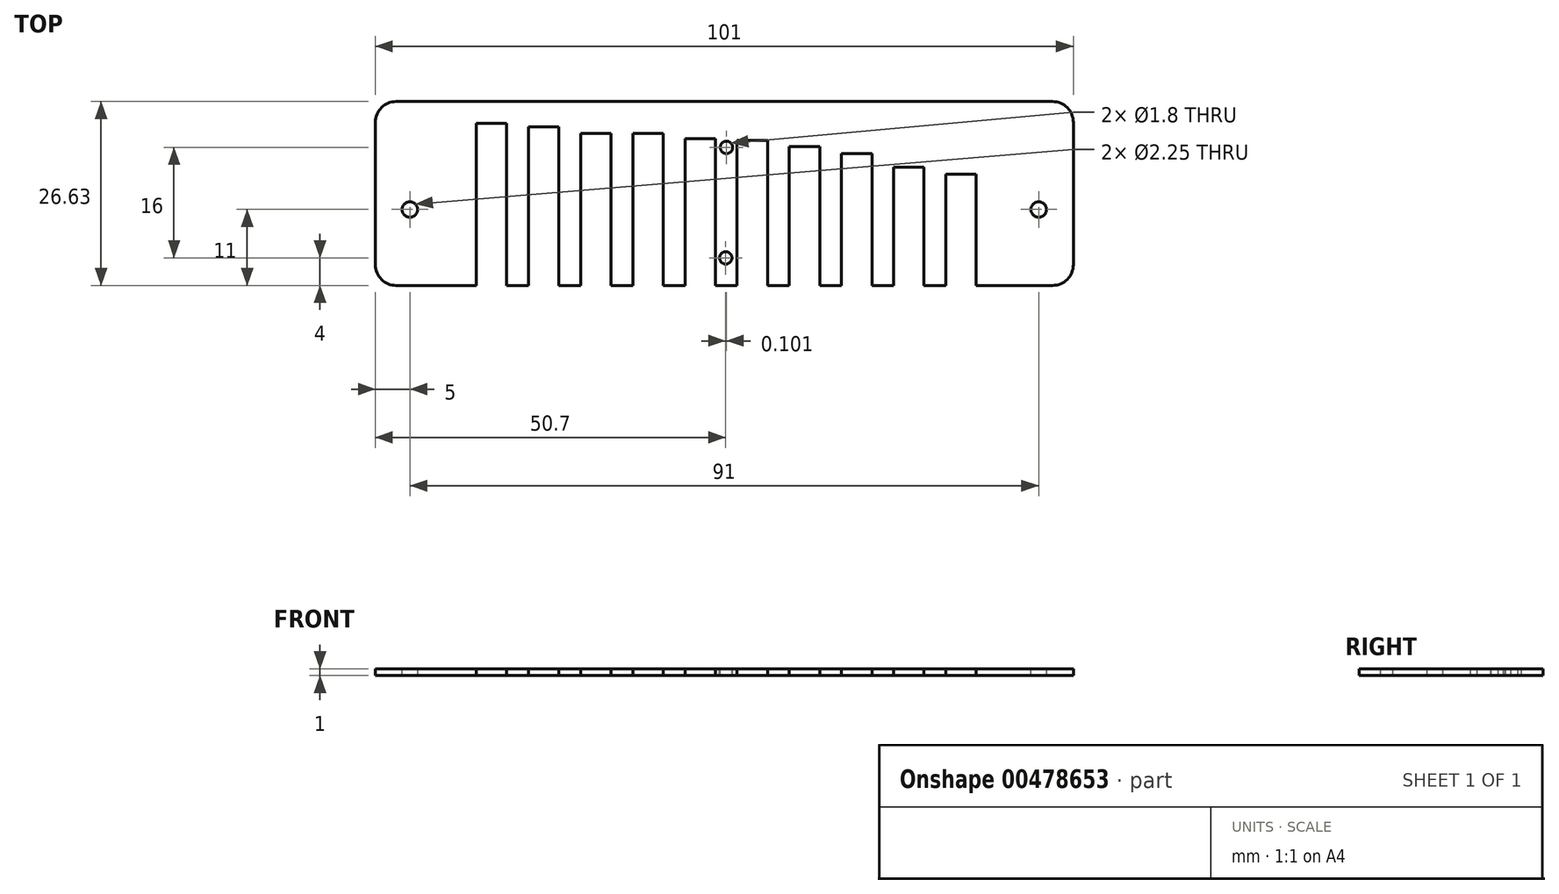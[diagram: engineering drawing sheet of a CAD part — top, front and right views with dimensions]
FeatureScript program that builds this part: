
annotation { "Feature Type Name" : "Feature", "Feature Type Description" : "" }
export const myFeature = defineFeature(function(context is Context, id is Id, definition is map)
    precondition{}
    {
        {
            var Q0;
            Q0=qCreatedBy(makeId("Right.planeOp"),FACE);
            var sketch = newSketch(context, id + "F0", { "sketchPlane" : qUnion([Q0])});
            skLineSegment(sketch, "E0.bottom", {"start": v(3, 0) * mm, "end": v(98, 0) * mm});
            skLineSegment(sketch, "E0.top", {"start": v(3, 26.63) * mm, "end": v(98, 26.63) * mm});
            skLineSegment(sketch, "E0.left", {"start": v(0, 3) * mm, "end": v(0, 23.63) * mm});
            skLineSegment(sketch, "E0.right", {"start": v(101, 3) * mm, "end": v(101, 23.63) * mm});
            skLineSegment(sketch, "E1.bottom", {"start": v(14.6, 26.63) * mm, "end": v(19, 26.63) * mm});
            skLineSegment(sketch, "E1.top", {"start": v(14.6, 3.13) * mm, "end": v(19, 3.13) * mm});
            skLineSegment(sketch, "E1.left", {"start": v(14.6, 26.63) * mm, "end": v(14.6, 3.13) * mm});
            skLineSegment(sketch, "E1.right", {"start": v(19, 26.63) * mm, "end": v(19, 3.13) * mm});
            skLineSegment(sketch, "E2.bottom", {"start": v(22.15, 26.63) * mm, "end": v(26.55, 26.63) * mm});
            skLineSegment(sketch, "E2.top", {"start": v(22.15, 3.63) * mm, "end": v(26.55, 3.63) * mm});
            skLineSegment(sketch, "E2.left", {"start": v(22.15, 26.63) * mm, "end": v(22.15, 3.63) * mm});
            skLineSegment(sketch, "E2.right", {"start": v(26.55, 26.63) * mm, "end": v(26.55, 3.63) * mm});
            skLineSegment(sketch, "E3.bottom", {"start": v(29.7, 26.63) * mm, "end": v(34.1, 26.63) * mm});
            skLineSegment(sketch, "E3.top", {"start": v(29.7, 4.63) * mm, "end": v(34.1, 4.63) * mm});
            skLineSegment(sketch, "E3.left", {"start": v(29.7, 26.63) * mm, "end": v(29.7, 4.63) * mm});
            skLineSegment(sketch, "E3.right", {"start": v(34.1, 26.63) * mm, "end": v(34.1, 4.63) * mm});
            skLineSegment(sketch, "E4.bottom", {"start": v(37.25, 26.63) * mm, "end": v(41.65, 26.63) * mm});
            skLineSegment(sketch, "E4.top", {"start": v(37.25, 4.63) * mm, "end": v(41.65, 4.63) * mm});
            skLineSegment(sketch, "E4.left", {"start": v(37.25, 26.63) * mm, "end": v(37.25, 4.63) * mm});
            skLineSegment(sketch, "E4.right", {"start": v(41.65, 26.63) * mm, "end": v(41.65, 4.63) * mm});
            skLineSegment(sketch, "E5.bottom", {"start": v(44.8, 26.63) * mm, "end": v(49.2, 26.63) * mm});
            skLineSegment(sketch, "E5.top", {"start": v(44.8, 5.4) * mm, "end": v(49.2, 5.4) * mm});
            skLineSegment(sketch, "E5.left", {"start": v(44.8, 26.63) * mm, "end": v(44.8, 5.4) * mm});
            skLineSegment(sketch, "E5.right", {"start": v(49.2, 26.63) * mm, "end": v(49.2, 5.4) * mm});
            skLineSegment(sketch, "E6.bottom", {"start": v(52.35, 26.63) * mm, "end": v(56.75, 26.63) * mm});
            skLineSegment(sketch, "E6.top", {"start": v(52.35, 5.63) * mm, "end": v(56.75, 5.63) * mm});
            skLineSegment(sketch, "E6.left", {"start": v(52.35, 26.63) * mm, "end": v(52.35, 5.63) * mm});
            skLineSegment(sketch, "E6.right", {"start": v(56.75, 26.63) * mm, "end": v(56.75, 5.63) * mm});
            skLineSegment(sketch, "E7.bottom", {"start": v(59.9, 26.63) * mm, "end": v(64.3, 26.63) * mm});
            skLineSegment(sketch, "E7.top", {"start": v(59.9, 6.5) * mm, "end": v(64.3, 6.5) * mm});
            skLineSegment(sketch, "E7.left", {"start": v(59.9, 26.63) * mm, "end": v(59.9, 6.5) * mm});
            skLineSegment(sketch, "E7.right", {"start": v(64.3, 26.63) * mm, "end": v(64.3, 6.5) * mm});
            skLineSegment(sketch, "E8.bottom", {"start": v(67.45, 26.63) * mm, "end": v(71.85, 26.63) * mm});
            skLineSegment(sketch, "E8.top", {"start": v(67.45, 7.56) * mm, "end": v(71.85, 7.56) * mm});
            skLineSegment(sketch, "E8.left", {"start": v(67.45, 26.63) * mm, "end": v(67.45, 7.56) * mm});
            skLineSegment(sketch, "E8.right", {"start": v(71.85, 26.63) * mm, "end": v(71.85, 7.56) * mm});
            skLineSegment(sketch, "E9.bottom", {"start": v(75, 26.63) * mm, "end": v(79.4, 26.63) * mm});
            skLineSegment(sketch, "E9.top", {"start": v(75, 9.52) * mm, "end": v(79.4, 9.52) * mm});
            skLineSegment(sketch, "E9.left", {"start": v(75, 26.63) * mm, "end": v(75, 9.52) * mm});
            skLineSegment(sketch, "E9.right", {"start": v(79.4, 26.63) * mm, "end": v(79.4, 9.52) * mm});
            skLineSegment(sketch, "E10.bottom", {"start": v(82.55, 26.63) * mm, "end": v(86.95, 26.63) * mm});
            skLineSegment(sketch, "E10.top", {"start": v(82.55, 10.52) * mm, "end": v(86.95, 10.52) * mm});
            skLineSegment(sketch, "E10.left", {"start": v(82.55, 26.63) * mm, "end": v(82.55, 10.52) * mm});
            skLineSegment(sketch, "E10.right", {"start": v(86.95, 26.63) * mm, "end": v(86.95, 10.52) * mm});
            skPoint(sketch, "E11.visualSharp", {"position": v(0, 26.63) * mm});
            skArc(sketch, "E11.filletArc", {"start": v(3, 26.63) * mm, "mid": v(0.88, 25.75) * mm, "end": v(0, 23.63) * mm});
            skPoint(sketch, "E12.visualSharp", {"position": v(0, 0) * mm});
            skArc(sketch, "E12.filletArc", {"start": v(0, 3) * mm, "mid": v(0.88, 0.88) * mm, "end": v(3, 0) * mm});
            skPoint(sketch, "E13.visualSharp", {"position": v(101, 26.63) * mm});
            skArc(sketch, "E13.filletArc", {"start": v(101, 23.63) * mm, "mid": v(100.12, 25.75) * mm, "end": v(98, 26.63) * mm});
            skPoint(sketch, "E14.visualSharp", {"position": v(101, 0) * mm});
            skArc(sketch, "E14.filletArc", {"start": v(98, 0) * mm, "mid": v(100.12, 0.88) * mm, "end": v(101, 3) * mm});
            skPoint(sketch, "E15", {"position": v(5, 15.63) * mm});
            skPoint(sketch, "E16", {"position": v(50.7, 22.63) * mm});
            skCircle(sketch, "E17", {"center": v(5, 15.63) * mm, "radius": 1.13 * mm});
            skCircle(sketch, "E18", {"center": v(96, 15.63) * mm, "radius": 1.13 * mm});
            skCircle(sketch, "E19", {"center": v(50.7, 22.63) * mm, "radius": 0.9 * mm});
            skPoint(sketch, "E20", {"position": v(50.8, 6.63) * mm});
            skCircle(sketch, "E21", {"center": v(50.8, 6.63) * mm, "radius": 0.9 * mm});
            skSolve(sketch);
        }
        {
            var Q0;
            Q0=makeQuery(id+"F0.imprint","IMPRINT",FACE,{"disambiguationData":[TD([[makeQuery(id+"F0.imprint","IMPRINT",EDGE,{"derivedFrom":sQuery(id+"F0.wireOp",EDGE,"E0.bottom")}),1.0]])]});
            extrude(context, id + "F1", {"entities" : qUnion([Q0]), "depth" : 1 * mm});
        }
        {
            var Q0;
            Q0=makeQuery(id+"F1.opExtrude","SWEPT_BODY",BODY,{"disambiguationData":[OSD([sQuery(id+"F0.wireOp",EDGE,"E0.bottom"),sQuery(id+"F0.wireOp",EDGE,"E0.top"),sQuery(id+"F0.wireOp",EDGE,"E0.left"),sQuery(id+"F0.wireOp",EDGE,"E0.right"),sQuery(id+"F0.wireOp",EDGE,"E1.top"),sQuery(id+"F0.wireOp",EDGE,"E1.left"),sQuery(id+"F0.wireOp",EDGE,"E1.right"),sQuery(id+"F0.wireOp",EDGE,"E2.top"),sQuery(id+"F0.wireOp",EDGE,"E2.left"),sQuery(id+"F0.wireOp",EDGE,"E2.right"),sQuery(id+"F0.wireOp",EDGE,"E3.top"),sQuery(id+"F0.wireOp",EDGE,"E3.left"),sQuery(id+"F0.wireOp",EDGE,"E3.right"),sQuery(id+"F0.wireOp",EDGE,"E4.top"),sQuery(id+"F0.wireOp",EDGE,"E4.left"),sQuery(id+"F0.wireOp",EDGE,"E4.right"),sQuery(id+"F0.wireOp",EDGE,"E5.top"),sQuery(id+"F0.wireOp",EDGE,"E5.left"),sQuery(id+"F0.wireOp",EDGE,"E5.right"),sQuery(id+"F0.wireOp",EDGE,"E6.top"),sQuery(id+"F0.wireOp",EDGE,"E6.left"),sQuery(id+"F0.wireOp",EDGE,"E6.right"),sQuery(id+"F0.wireOp",EDGE,"E7.top"),sQuery(id+"F0.wireOp",EDGE,"E7.left"),sQuery(id+"F0.wireOp",EDGE,"E7.right"),sQuery(id+"F0.wireOp",EDGE,"E8.top"),sQuery(id+"F0.wireOp",EDGE,"E8.left"),sQuery(id+"F0.wireOp",EDGE,"E8.right"),sQuery(id+"F0.wireOp",EDGE,"E9.top"),sQuery(id+"F0.wireOp",EDGE,"E9.left"),sQuery(id+"F0.wireOp",EDGE,"E9.right"),sQuery(id+"F0.wireOp",EDGE,"E10.top"),sQuery(id+"F0.wireOp",EDGE,"E10.left"),sQuery(id+"F0.wireOp",EDGE,"E10.right"),sQuery(id+"F0.wireOp",EDGE,"E11.filletArc"),sQuery(id+"F0.wireOp",EDGE,"E12.filletArc"),sQuery(id+"F0.wireOp",EDGE,"E13.filletArc"),sQuery(id+"F0.wireOp",EDGE,"E14.filletArc"),sQuery(id+"F0.wireOp",EDGE,"E17"),sQuery(id+"F0.wireOp",EDGE,"E18"),sQuery(id+"F0.wireOp",EDGE,"E19"),sQuery(id+"F0.wireOp",EDGE,"E21")])]});
            var Q1;
            Q1=makeQuery(id+"F1.opExtrude","CAP_EDGE",EDGE,{"disambiguationData":[OSD([sQuery(id+"F0.wireOp",EDGE,"E0.bottom")])],"isStart":false});
            transform(context, id + "F2", {"entities" : qUnion([Q0]), "transformType" : TransformType.ROTATION, "transformAxis" : qUnion([Q1]), "angle" : 90 * degree, "makeCopy" : false});
        }
        {
            var Q0;
            Q0=makeQuery(id+"F1.opExtrude","SWEPT_BODY",BODY,{"disambiguationData":[OSD([sQuery(id+"F0.wireOp",EDGE,"E0.bottom"),sQuery(id+"F0.wireOp",EDGE,"E0.top"),sQuery(id+"F0.wireOp",EDGE,"E0.left"),sQuery(id+"F0.wireOp",EDGE,"E0.right"),sQuery(id+"F0.wireOp",EDGE,"E1.top"),sQuery(id+"F0.wireOp",EDGE,"E1.left"),sQuery(id+"F0.wireOp",EDGE,"E1.right"),sQuery(id+"F0.wireOp",EDGE,"E2.top"),sQuery(id+"F0.wireOp",EDGE,"E2.left"),sQuery(id+"F0.wireOp",EDGE,"E2.right"),sQuery(id+"F0.wireOp",EDGE,"E3.top"),sQuery(id+"F0.wireOp",EDGE,"E3.left"),sQuery(id+"F0.wireOp",EDGE,"E3.right"),sQuery(id+"F0.wireOp",EDGE,"E4.top"),sQuery(id+"F0.wireOp",EDGE,"E4.left"),sQuery(id+"F0.wireOp",EDGE,"E4.right"),sQuery(id+"F0.wireOp",EDGE,"E5.top"),sQuery(id+"F0.wireOp",EDGE,"E5.left"),sQuery(id+"F0.wireOp",EDGE,"E5.right"),sQuery(id+"F0.wireOp",EDGE,"E6.top"),sQuery(id+"F0.wireOp",EDGE,"E6.left"),sQuery(id+"F0.wireOp",EDGE,"E6.right"),sQuery(id+"F0.wireOp",EDGE,"E7.top"),sQuery(id+"F0.wireOp",EDGE,"E7.left"),sQuery(id+"F0.wireOp",EDGE,"E7.right"),sQuery(id+"F0.wireOp",EDGE,"E8.top"),sQuery(id+"F0.wireOp",EDGE,"E8.left"),sQuery(id+"F0.wireOp",EDGE,"E8.right"),sQuery(id+"F0.wireOp",EDGE,"E9.top"),sQuery(id+"F0.wireOp",EDGE,"E9.left"),sQuery(id+"F0.wireOp",EDGE,"E9.right"),sQuery(id+"F0.wireOp",EDGE,"E10.top"),sQuery(id+"F0.wireOp",EDGE,"E10.left"),sQuery(id+"F0.wireOp",EDGE,"E10.right"),sQuery(id+"F0.wireOp",EDGE,"E11.filletArc"),sQuery(id+"F0.wireOp",EDGE,"E12.filletArc"),sQuery(id+"F0.wireOp",EDGE,"E13.filletArc"),sQuery(id+"F0.wireOp",EDGE,"E14.filletArc"),sQuery(id+"F0.wireOp",EDGE,"E17"),sQuery(id+"F0.wireOp",EDGE,"E18"),sQuery(id+"F0.wireOp",EDGE,"E19"),sQuery(id+"F0.wireOp",EDGE,"E21")])]});
            var Q1;
            Q1=makeQuery(id+"F1.opExtrude","SWEPT_FACE",FACE,{"disambiguationData":[OSD([sQuery(id+"F0.wireOp",EDGE,"E12.filletArc")])]});
            transform(context, id + "F3", {"entities" : qUnion([Q0]), "transformType" : TransformType.ROTATION, "transformAxis" : qUnion([Q1]), "angle" : 90 * degree, "oppositeDirection" : true, "makeCopy" : false});
        }
        {
            var Q0;
            Q0=makeQuery(id+"FeItU8t7BcqmXxs_1.opPattern","COPY",BODY,{"derivedFrom":makeQuery(id+"FirfgJDHHkA21Hh_1.opPattern","COPY",BODY,{"derivedFrom":makeQuery(id+"Flst8gmBcSAihEz_1.opPattern","COPY",BODY,{"derivedFrom":makeQuery(id+"FnchQCX3KFHkyZE_1.opPattern","COPY",BODY,{"derivedFrom":makeQuery(id+"FnXCqMF8rCCX5tp_1.opPattern","COPY",BODY,{"derivedFrom":makeQuery(id+"FpTvk6VpooPmInK_1.opPattern","COPY",BODY,{"derivedFrom":makeQuery(id+"FDAv0ZJfrHdLi5i_1.opPattern","COPY",BODY,{"derivedFrom":makeQuery(id+"FECZTDOQryJ9ywm_1.opPattern","COPY",BODY,{"derivedFrom":makeQuery(id+"F1.opExtrude","SWEPT_BODY",BODY,{"disambiguationData":[OSD([sQuery(id+"F0.wireOp",EDGE,"E0.bottom"),sQuery(id+"F0.wireOp",EDGE,"E0.top"),sQuery(id+"F0.wireOp",EDGE,"E0.left"),sQuery(id+"F0.wireOp",EDGE,"E0.right"),sQuery(id+"F0.wireOp",EDGE,"E1.top"),sQuery(id+"F0.wireOp",EDGE,"E1.left"),sQuery(id+"F0.wireOp",EDGE,"E1.right"),sQuery(id+"F0.wireOp",EDGE,"E2.top"),sQuery(id+"F0.wireOp",EDGE,"E2.left"),sQuery(id+"F0.wireOp",EDGE,"E2.right"),sQuery(id+"F0.wireOp",EDGE,"E3.top"),sQuery(id+"F0.wireOp",EDGE,"E3.left"),sQuery(id+"F0.wireOp",EDGE,"E3.right"),sQuery(id+"F0.wireOp",EDGE,"E4.top"),sQuery(id+"F0.wireOp",EDGE,"E4.left"),sQuery(id+"F0.wireOp",EDGE,"E4.right"),sQuery(id+"F0.wireOp",EDGE,"E5.top"),sQuery(id+"F0.wireOp",EDGE,"E5.left"),sQuery(id+"F0.wireOp",EDGE,"E5.right"),sQuery(id+"F0.wireOp",EDGE,"E6.top"),sQuery(id+"F0.wireOp",EDGE,"E6.left"),sQuery(id+"F0.wireOp",EDGE,"E6.right"),sQuery(id+"F0.wireOp",EDGE,"E7.top"),sQuery(id+"F0.wireOp",EDGE,"E7.left"),sQuery(id+"F0.wireOp",EDGE,"E7.right"),sQuery(id+"F0.wireOp",EDGE,"E8.top"),sQuery(id+"F0.wireOp",EDGE,"E8.left"),sQuery(id+"F0.wireOp",EDGE,"E8.right"),sQuery(id+"F0.wireOp",EDGE,"E9.top"),sQuery(id+"F0.wireOp",EDGE,"E9.left"),sQuery(id+"F0.wireOp",EDGE,"E9.right"),sQuery(id+"F0.wireOp",EDGE,"E10.top"),sQuery(id+"F0.wireOp",EDGE,"E10.left"),sQuery(id+"F0.wireOp",EDGE,"E10.right"),sQuery(id+"F0.wireOp",EDGE,"E11.filletArc"),sQuery(id+"F0.wireOp",EDGE,"E12.filletArc"),sQuery(id+"F0.wireOp",EDGE,"E13.filletArc"),sQuery(id+"F0.wireOp",EDGE,"E14.filletArc"),sQuery(id+"F0.wireOp",EDGE,"E17"),sQuery(id+"F0.wireOp",EDGE,"E18"),sQuery(id+"F0.wireOp",EDGE,"E19"),sQuery(id+"F0.wireOp",EDGE,"E21")])]}),"instanceName":"1"}),"instanceName":"1"}),"instanceName":"1"}),"instanceName":"1"}),"instanceName":"1"}),"instanceName":"1"}),"instanceName":"1"}),"instanceName":"1"});
            var Q1;
            Q1=makeQuery(id+"FirfgJDHHkA21Hh_1.opPattern","COPY",BODY,{"derivedFrom":makeQuery(id+"Flst8gmBcSAihEz_1.opPattern","COPY",BODY,{"derivedFrom":makeQuery(id+"FnchQCX3KFHkyZE_1.opPattern","COPY",BODY,{"derivedFrom":makeQuery(id+"FnXCqMF8rCCX5tp_1.opPattern","COPY",BODY,{"derivedFrom":makeQuery(id+"FpTvk6VpooPmInK_1.opPattern","COPY",BODY,{"derivedFrom":makeQuery(id+"FDAv0ZJfrHdLi5i_1.opPattern","COPY",BODY,{"derivedFrom":makeQuery(id+"FECZTDOQryJ9ywm_1.opPattern","COPY",BODY,{"derivedFrom":makeQuery(id+"F1.opExtrude","SWEPT_BODY",BODY,{"disambiguationData":[OSD([sQuery(id+"F0.wireOp",EDGE,"E0.bottom"),sQuery(id+"F0.wireOp",EDGE,"E0.top"),sQuery(id+"F0.wireOp",EDGE,"E0.left"),sQuery(id+"F0.wireOp",EDGE,"E0.right"),sQuery(id+"F0.wireOp",EDGE,"E1.top"),sQuery(id+"F0.wireOp",EDGE,"E1.left"),sQuery(id+"F0.wireOp",EDGE,"E1.right"),sQuery(id+"F0.wireOp",EDGE,"E2.top"),sQuery(id+"F0.wireOp",EDGE,"E2.left"),sQuery(id+"F0.wireOp",EDGE,"E2.right"),sQuery(id+"F0.wireOp",EDGE,"E3.top"),sQuery(id+"F0.wireOp",EDGE,"E3.left"),sQuery(id+"F0.wireOp",EDGE,"E3.right"),sQuery(id+"F0.wireOp",EDGE,"E4.top"),sQuery(id+"F0.wireOp",EDGE,"E4.left"),sQuery(id+"F0.wireOp",EDGE,"E4.right"),sQuery(id+"F0.wireOp",EDGE,"E5.top"),sQuery(id+"F0.wireOp",EDGE,"E5.left"),sQuery(id+"F0.wireOp",EDGE,"E5.right"),sQuery(id+"F0.wireOp",EDGE,"E6.top"),sQuery(id+"F0.wireOp",EDGE,"E6.left"),sQuery(id+"F0.wireOp",EDGE,"E6.right"),sQuery(id+"F0.wireOp",EDGE,"E7.top"),sQuery(id+"F0.wireOp",EDGE,"E7.left"),sQuery(id+"F0.wireOp",EDGE,"E7.right"),sQuery(id+"F0.wireOp",EDGE,"E8.top"),sQuery(id+"F0.wireOp",EDGE,"E8.left"),sQuery(id+"F0.wireOp",EDGE,"E8.right"),sQuery(id+"F0.wireOp",EDGE,"E9.top"),sQuery(id+"F0.wireOp",EDGE,"E9.left"),sQuery(id+"F0.wireOp",EDGE,"E9.right"),sQuery(id+"F0.wireOp",EDGE,"E10.top"),sQuery(id+"F0.wireOp",EDGE,"E10.left"),sQuery(id+"F0.wireOp",EDGE,"E10.right"),sQuery(id+"F0.wireOp",EDGE,"E11.filletArc"),sQuery(id+"F0.wireOp",EDGE,"E12.filletArc"),sQuery(id+"F0.wireOp",EDGE,"E13.filletArc"),sQuery(id+"F0.wireOp",EDGE,"E14.filletArc"),sQuery(id+"F0.wireOp",EDGE,"E17"),sQuery(id+"F0.wireOp",EDGE,"E18"),sQuery(id+"F0.wireOp",EDGE,"E19"),sQuery(id+"F0.wireOp",EDGE,"E21")])]}),"instanceName":"1"}),"instanceName":"1"}),"instanceName":"1"}),"instanceName":"1"}),"instanceName":"1"}),"instanceName":"1"}),"instanceName":"1"});
            var Q2;
            Q2=makeQuery(id+"Flst8gmBcSAihEz_1.opPattern","COPY",BODY,{"derivedFrom":makeQuery(id+"FnchQCX3KFHkyZE_1.opPattern","COPY",BODY,{"derivedFrom":makeQuery(id+"FnXCqMF8rCCX5tp_1.opPattern","COPY",BODY,{"derivedFrom":makeQuery(id+"FpTvk6VpooPmInK_1.opPattern","COPY",BODY,{"derivedFrom":makeQuery(id+"FDAv0ZJfrHdLi5i_1.opPattern","COPY",BODY,{"derivedFrom":makeQuery(id+"FECZTDOQryJ9ywm_1.opPattern","COPY",BODY,{"derivedFrom":makeQuery(id+"F1.opExtrude","SWEPT_BODY",BODY,{"disambiguationData":[OSD([sQuery(id+"F0.wireOp",EDGE,"E0.bottom"),sQuery(id+"F0.wireOp",EDGE,"E0.top"),sQuery(id+"F0.wireOp",EDGE,"E0.left"),sQuery(id+"F0.wireOp",EDGE,"E0.right"),sQuery(id+"F0.wireOp",EDGE,"E1.top"),sQuery(id+"F0.wireOp",EDGE,"E1.left"),sQuery(id+"F0.wireOp",EDGE,"E1.right"),sQuery(id+"F0.wireOp",EDGE,"E2.top"),sQuery(id+"F0.wireOp",EDGE,"E2.left"),sQuery(id+"F0.wireOp",EDGE,"E2.right"),sQuery(id+"F0.wireOp",EDGE,"E3.top"),sQuery(id+"F0.wireOp",EDGE,"E3.left"),sQuery(id+"F0.wireOp",EDGE,"E3.right"),sQuery(id+"F0.wireOp",EDGE,"E4.top"),sQuery(id+"F0.wireOp",EDGE,"E4.left"),sQuery(id+"F0.wireOp",EDGE,"E4.right"),sQuery(id+"F0.wireOp",EDGE,"E5.top"),sQuery(id+"F0.wireOp",EDGE,"E5.left"),sQuery(id+"F0.wireOp",EDGE,"E5.right"),sQuery(id+"F0.wireOp",EDGE,"E6.top"),sQuery(id+"F0.wireOp",EDGE,"E6.left"),sQuery(id+"F0.wireOp",EDGE,"E6.right"),sQuery(id+"F0.wireOp",EDGE,"E7.top"),sQuery(id+"F0.wireOp",EDGE,"E7.left"),sQuery(id+"F0.wireOp",EDGE,"E7.right"),sQuery(id+"F0.wireOp",EDGE,"E8.top"),sQuery(id+"F0.wireOp",EDGE,"E8.left"),sQuery(id+"F0.wireOp",EDGE,"E8.right"),sQuery(id+"F0.wireOp",EDGE,"E9.top"),sQuery(id+"F0.wireOp",EDGE,"E9.left"),sQuery(id+"F0.wireOp",EDGE,"E9.right"),sQuery(id+"F0.wireOp",EDGE,"E10.top"),sQuery(id+"F0.wireOp",EDGE,"E10.left"),sQuery(id+"F0.wireOp",EDGE,"E10.right"),sQuery(id+"F0.wireOp",EDGE,"E11.filletArc"),sQuery(id+"F0.wireOp",EDGE,"E12.filletArc"),sQuery(id+"F0.wireOp",EDGE,"E13.filletArc"),sQuery(id+"F0.wireOp",EDGE,"E14.filletArc"),sQuery(id+"F0.wireOp",EDGE,"E17"),sQuery(id+"F0.wireOp",EDGE,"E18"),sQuery(id+"F0.wireOp",EDGE,"E19"),sQuery(id+"F0.wireOp",EDGE,"E21")])]}),"instanceName":"1"}),"instanceName":"1"}),"instanceName":"1"}),"instanceName":"1"}),"instanceName":"1"}),"instanceName":"1"});
            var Q3;
            Q3=makeQuery(id+"FnchQCX3KFHkyZE_1.opPattern","COPY",BODY,{"derivedFrom":makeQuery(id+"FnXCqMF8rCCX5tp_1.opPattern","COPY",BODY,{"derivedFrom":makeQuery(id+"FpTvk6VpooPmInK_1.opPattern","COPY",BODY,{"derivedFrom":makeQuery(id+"FDAv0ZJfrHdLi5i_1.opPattern","COPY",BODY,{"derivedFrom":makeQuery(id+"FECZTDOQryJ9ywm_1.opPattern","COPY",BODY,{"derivedFrom":makeQuery(id+"F1.opExtrude","SWEPT_BODY",BODY,{"disambiguationData":[OSD([sQuery(id+"F0.wireOp",EDGE,"E0.bottom"),sQuery(id+"F0.wireOp",EDGE,"E0.top"),sQuery(id+"F0.wireOp",EDGE,"E0.left"),sQuery(id+"F0.wireOp",EDGE,"E0.right"),sQuery(id+"F0.wireOp",EDGE,"E1.top"),sQuery(id+"F0.wireOp",EDGE,"E1.left"),sQuery(id+"F0.wireOp",EDGE,"E1.right"),sQuery(id+"F0.wireOp",EDGE,"E2.top"),sQuery(id+"F0.wireOp",EDGE,"E2.left"),sQuery(id+"F0.wireOp",EDGE,"E2.right"),sQuery(id+"F0.wireOp",EDGE,"E3.top"),sQuery(id+"F0.wireOp",EDGE,"E3.left"),sQuery(id+"F0.wireOp",EDGE,"E3.right"),sQuery(id+"F0.wireOp",EDGE,"E4.top"),sQuery(id+"F0.wireOp",EDGE,"E4.left"),sQuery(id+"F0.wireOp",EDGE,"E4.right"),sQuery(id+"F0.wireOp",EDGE,"E5.top"),sQuery(id+"F0.wireOp",EDGE,"E5.left"),sQuery(id+"F0.wireOp",EDGE,"E5.right"),sQuery(id+"F0.wireOp",EDGE,"E6.top"),sQuery(id+"F0.wireOp",EDGE,"E6.left"),sQuery(id+"F0.wireOp",EDGE,"E6.right"),sQuery(id+"F0.wireOp",EDGE,"E7.top"),sQuery(id+"F0.wireOp",EDGE,"E7.left"),sQuery(id+"F0.wireOp",EDGE,"E7.right"),sQuery(id+"F0.wireOp",EDGE,"E8.top"),sQuery(id+"F0.wireOp",EDGE,"E8.left"),sQuery(id+"F0.wireOp",EDGE,"E8.right"),sQuery(id+"F0.wireOp",EDGE,"E9.top"),sQuery(id+"F0.wireOp",EDGE,"E9.left"),sQuery(id+"F0.wireOp",EDGE,"E9.right"),sQuery(id+"F0.wireOp",EDGE,"E10.top"),sQuery(id+"F0.wireOp",EDGE,"E10.left"),sQuery(id+"F0.wireOp",EDGE,"E10.right"),sQuery(id+"F0.wireOp",EDGE,"E11.filletArc"),sQuery(id+"F0.wireOp",EDGE,"E12.filletArc"),sQuery(id+"F0.wireOp",EDGE,"E13.filletArc"),sQuery(id+"F0.wireOp",EDGE,"E14.filletArc"),sQuery(id+"F0.wireOp",EDGE,"E17"),sQuery(id+"F0.wireOp",EDGE,"E18"),sQuery(id+"F0.wireOp",EDGE,"E19"),sQuery(id+"F0.wireOp",EDGE,"E21")])]}),"instanceName":"1"}),"instanceName":"1"}),"instanceName":"1"}),"instanceName":"1"}),"instanceName":"1"});
            var Q4;
            Q4=makeQuery(id+"FnXCqMF8rCCX5tp_1.opPattern","COPY",BODY,{"derivedFrom":makeQuery(id+"FpTvk6VpooPmInK_1.opPattern","COPY",BODY,{"derivedFrom":makeQuery(id+"FDAv0ZJfrHdLi5i_1.opPattern","COPY",BODY,{"derivedFrom":makeQuery(id+"FECZTDOQryJ9ywm_1.opPattern","COPY",BODY,{"derivedFrom":makeQuery(id+"F1.opExtrude","SWEPT_BODY",BODY,{"disambiguationData":[OSD([sQuery(id+"F0.wireOp",EDGE,"E0.bottom"),sQuery(id+"F0.wireOp",EDGE,"E0.top"),sQuery(id+"F0.wireOp",EDGE,"E0.left"),sQuery(id+"F0.wireOp",EDGE,"E0.right"),sQuery(id+"F0.wireOp",EDGE,"E1.top"),sQuery(id+"F0.wireOp",EDGE,"E1.left"),sQuery(id+"F0.wireOp",EDGE,"E1.right"),sQuery(id+"F0.wireOp",EDGE,"E2.top"),sQuery(id+"F0.wireOp",EDGE,"E2.left"),sQuery(id+"F0.wireOp",EDGE,"E2.right"),sQuery(id+"F0.wireOp",EDGE,"E3.top"),sQuery(id+"F0.wireOp",EDGE,"E3.left"),sQuery(id+"F0.wireOp",EDGE,"E3.right"),sQuery(id+"F0.wireOp",EDGE,"E4.top"),sQuery(id+"F0.wireOp",EDGE,"E4.left"),sQuery(id+"F0.wireOp",EDGE,"E4.right"),sQuery(id+"F0.wireOp",EDGE,"E5.top"),sQuery(id+"F0.wireOp",EDGE,"E5.left"),sQuery(id+"F0.wireOp",EDGE,"E5.right"),sQuery(id+"F0.wireOp",EDGE,"E6.top"),sQuery(id+"F0.wireOp",EDGE,"E6.left"),sQuery(id+"F0.wireOp",EDGE,"E6.right"),sQuery(id+"F0.wireOp",EDGE,"E7.top"),sQuery(id+"F0.wireOp",EDGE,"E7.left"),sQuery(id+"F0.wireOp",EDGE,"E7.right"),sQuery(id+"F0.wireOp",EDGE,"E8.top"),sQuery(id+"F0.wireOp",EDGE,"E8.left"),sQuery(id+"F0.wireOp",EDGE,"E8.right"),sQuery(id+"F0.wireOp",EDGE,"E9.top"),sQuery(id+"F0.wireOp",EDGE,"E9.left"),sQuery(id+"F0.wireOp",EDGE,"E9.right"),sQuery(id+"F0.wireOp",EDGE,"E10.top"),sQuery(id+"F0.wireOp",EDGE,"E10.left"),sQuery(id+"F0.wireOp",EDGE,"E10.right"),sQuery(id+"F0.wireOp",EDGE,"E11.filletArc"),sQuery(id+"F0.wireOp",EDGE,"E12.filletArc"),sQuery(id+"F0.wireOp",EDGE,"E13.filletArc"),sQuery(id+"F0.wireOp",EDGE,"E14.filletArc"),sQuery(id+"F0.wireOp",EDGE,"E17"),sQuery(id+"F0.wireOp",EDGE,"E18"),sQuery(id+"F0.wireOp",EDGE,"E19"),sQuery(id+"F0.wireOp",EDGE,"E21")])]}),"instanceName":"1"}),"instanceName":"1"}),"instanceName":"1"}),"instanceName":"1"});
            var Q5;
            Q5=makeQuery(id+"F1.opExtrude","SWEPT_BODY",BODY,{"disambiguationData":[OSD([sQuery(id+"F0.wireOp",EDGE,"E0.bottom"),sQuery(id+"F0.wireOp",EDGE,"E0.top"),sQuery(id+"F0.wireOp",EDGE,"E0.left"),sQuery(id+"F0.wireOp",EDGE,"E0.right"),sQuery(id+"F0.wireOp",EDGE,"E1.top"),sQuery(id+"F0.wireOp",EDGE,"E1.left"),sQuery(id+"F0.wireOp",EDGE,"E1.right"),sQuery(id+"F0.wireOp",EDGE,"E2.top"),sQuery(id+"F0.wireOp",EDGE,"E2.left"),sQuery(id+"F0.wireOp",EDGE,"E2.right"),sQuery(id+"F0.wireOp",EDGE,"E3.top"),sQuery(id+"F0.wireOp",EDGE,"E3.left"),sQuery(id+"F0.wireOp",EDGE,"E3.right"),sQuery(id+"F0.wireOp",EDGE,"E4.top"),sQuery(id+"F0.wireOp",EDGE,"E4.left"),sQuery(id+"F0.wireOp",EDGE,"E4.right"),sQuery(id+"F0.wireOp",EDGE,"E5.top"),sQuery(id+"F0.wireOp",EDGE,"E5.left"),sQuery(id+"F0.wireOp",EDGE,"E5.right"),sQuery(id+"F0.wireOp",EDGE,"E6.top"),sQuery(id+"F0.wireOp",EDGE,"E6.left"),sQuery(id+"F0.wireOp",EDGE,"E6.right"),sQuery(id+"F0.wireOp",EDGE,"E7.top"),sQuery(id+"F0.wireOp",EDGE,"E7.left"),sQuery(id+"F0.wireOp",EDGE,"E7.right"),sQuery(id+"F0.wireOp",EDGE,"E8.top"),sQuery(id+"F0.wireOp",EDGE,"E8.left"),sQuery(id+"F0.wireOp",EDGE,"E8.right"),sQuery(id+"F0.wireOp",EDGE,"E9.top"),sQuery(id+"F0.wireOp",EDGE,"E9.left"),sQuery(id+"F0.wireOp",EDGE,"E9.right"),sQuery(id+"F0.wireOp",EDGE,"E10.top"),sQuery(id+"F0.wireOp",EDGE,"E10.left"),sQuery(id+"F0.wireOp",EDGE,"E10.right"),sQuery(id+"F0.wireOp",EDGE,"E11.filletArc"),sQuery(id+"F0.wireOp",EDGE,"E12.filletArc"),sQuery(id+"F0.wireOp",EDGE,"E13.filletArc"),sQuery(id+"F0.wireOp",EDGE,"E14.filletArc"),sQuery(id+"F0.wireOp",EDGE,"E17"),sQuery(id+"F0.wireOp",EDGE,"E18"),sQuery(id+"F0.wireOp",EDGE,"E19"),sQuery(id+"F0.wireOp",EDGE,"E21")])]});
            var Q6;
            Q6=makeQuery(id+"FpTvk6VpooPmInK_1.opPattern","COPY",BODY,{"derivedFrom":makeQuery(id+"FDAv0ZJfrHdLi5i_1.opPattern","COPY",BODY,{"derivedFrom":makeQuery(id+"FECZTDOQryJ9ywm_1.opPattern","COPY",BODY,{"derivedFrom":makeQuery(id+"F1.opExtrude","SWEPT_BODY",BODY,{"disambiguationData":[OSD([sQuery(id+"F0.wireOp",EDGE,"E0.bottom"),sQuery(id+"F0.wireOp",EDGE,"E0.top"),sQuery(id+"F0.wireOp",EDGE,"E0.left"),sQuery(id+"F0.wireOp",EDGE,"E0.right"),sQuery(id+"F0.wireOp",EDGE,"E1.top"),sQuery(id+"F0.wireOp",EDGE,"E1.left"),sQuery(id+"F0.wireOp",EDGE,"E1.right"),sQuery(id+"F0.wireOp",EDGE,"E2.top"),sQuery(id+"F0.wireOp",EDGE,"E2.left"),sQuery(id+"F0.wireOp",EDGE,"E2.right"),sQuery(id+"F0.wireOp",EDGE,"E3.top"),sQuery(id+"F0.wireOp",EDGE,"E3.left"),sQuery(id+"F0.wireOp",EDGE,"E3.right"),sQuery(id+"F0.wireOp",EDGE,"E4.top"),sQuery(id+"F0.wireOp",EDGE,"E4.left"),sQuery(id+"F0.wireOp",EDGE,"E4.right"),sQuery(id+"F0.wireOp",EDGE,"E5.top"),sQuery(id+"F0.wireOp",EDGE,"E5.left"),sQuery(id+"F0.wireOp",EDGE,"E5.right"),sQuery(id+"F0.wireOp",EDGE,"E6.top"),sQuery(id+"F0.wireOp",EDGE,"E6.left"),sQuery(id+"F0.wireOp",EDGE,"E6.right"),sQuery(id+"F0.wireOp",EDGE,"E7.top"),sQuery(id+"F0.wireOp",EDGE,"E7.left"),sQuery(id+"F0.wireOp",EDGE,"E7.right"),sQuery(id+"F0.wireOp",EDGE,"E8.top"),sQuery(id+"F0.wireOp",EDGE,"E8.left"),sQuery(id+"F0.wireOp",EDGE,"E8.right"),sQuery(id+"F0.wireOp",EDGE,"E9.top"),sQuery(id+"F0.wireOp",EDGE,"E9.left"),sQuery(id+"F0.wireOp",EDGE,"E9.right"),sQuery(id+"F0.wireOp",EDGE,"E10.top"),sQuery(id+"F0.wireOp",EDGE,"E10.left"),sQuery(id+"F0.wireOp",EDGE,"E10.right"),sQuery(id+"F0.wireOp",EDGE,"E11.filletArc"),sQuery(id+"F0.wireOp",EDGE,"E12.filletArc"),sQuery(id+"F0.wireOp",EDGE,"E13.filletArc"),sQuery(id+"F0.wireOp",EDGE,"E14.filletArc"),sQuery(id+"F0.wireOp",EDGE,"E17"),sQuery(id+"F0.wireOp",EDGE,"E18"),sQuery(id+"F0.wireOp",EDGE,"E19"),sQuery(id+"F0.wireOp",EDGE,"E21")])]}),"instanceName":"1"}),"instanceName":"1"}),"instanceName":"1"});
            var Q7;
            Q7=makeQuery(id+"FDAv0ZJfrHdLi5i_1.opPattern","COPY",BODY,{"derivedFrom":makeQuery(id+"FECZTDOQryJ9ywm_1.opPattern","COPY",BODY,{"derivedFrom":makeQuery(id+"F1.opExtrude","SWEPT_BODY",BODY,{"disambiguationData":[OSD([sQuery(id+"F0.wireOp",EDGE,"E0.bottom"),sQuery(id+"F0.wireOp",EDGE,"E0.top"),sQuery(id+"F0.wireOp",EDGE,"E0.left"),sQuery(id+"F0.wireOp",EDGE,"E0.right"),sQuery(id+"F0.wireOp",EDGE,"E1.top"),sQuery(id+"F0.wireOp",EDGE,"E1.left"),sQuery(id+"F0.wireOp",EDGE,"E1.right"),sQuery(id+"F0.wireOp",EDGE,"E2.top"),sQuery(id+"F0.wireOp",EDGE,"E2.left"),sQuery(id+"F0.wireOp",EDGE,"E2.right"),sQuery(id+"F0.wireOp",EDGE,"E3.top"),sQuery(id+"F0.wireOp",EDGE,"E3.left"),sQuery(id+"F0.wireOp",EDGE,"E3.right"),sQuery(id+"F0.wireOp",EDGE,"E4.top"),sQuery(id+"F0.wireOp",EDGE,"E4.left"),sQuery(id+"F0.wireOp",EDGE,"E4.right"),sQuery(id+"F0.wireOp",EDGE,"E5.top"),sQuery(id+"F0.wireOp",EDGE,"E5.left"),sQuery(id+"F0.wireOp",EDGE,"E5.right"),sQuery(id+"F0.wireOp",EDGE,"E6.top"),sQuery(id+"F0.wireOp",EDGE,"E6.left"),sQuery(id+"F0.wireOp",EDGE,"E6.right"),sQuery(id+"F0.wireOp",EDGE,"E7.top"),sQuery(id+"F0.wireOp",EDGE,"E7.left"),sQuery(id+"F0.wireOp",EDGE,"E7.right"),sQuery(id+"F0.wireOp",EDGE,"E8.top"),sQuery(id+"F0.wireOp",EDGE,"E8.left"),sQuery(id+"F0.wireOp",EDGE,"E8.right"),sQuery(id+"F0.wireOp",EDGE,"E9.top"),sQuery(id+"F0.wireOp",EDGE,"E9.left"),sQuery(id+"F0.wireOp",EDGE,"E9.right"),sQuery(id+"F0.wireOp",EDGE,"E10.top"),sQuery(id+"F0.wireOp",EDGE,"E10.left"),sQuery(id+"F0.wireOp",EDGE,"E10.right"),sQuery(id+"F0.wireOp",EDGE,"E11.filletArc"),sQuery(id+"F0.wireOp",EDGE,"E12.filletArc"),sQuery(id+"F0.wireOp",EDGE,"E13.filletArc"),sQuery(id+"F0.wireOp",EDGE,"E14.filletArc"),sQuery(id+"F0.wireOp",EDGE,"E17"),sQuery(id+"F0.wireOp",EDGE,"E18"),sQuery(id+"F0.wireOp",EDGE,"E19"),sQuery(id+"F0.wireOp",EDGE,"E21")])]}),"instanceName":"1"}),"instanceName":"1"});
            var Q8;
            Q8=makeQuery(id+"FECZTDOQryJ9ywm_1.opPattern","COPY",BODY,{"derivedFrom":makeQuery(id+"F1.opExtrude","SWEPT_BODY",BODY,{"disambiguationData":[OSD([sQuery(id+"F0.wireOp",EDGE,"E0.bottom"),sQuery(id+"F0.wireOp",EDGE,"E0.top"),sQuery(id+"F0.wireOp",EDGE,"E0.left"),sQuery(id+"F0.wireOp",EDGE,"E0.right"),sQuery(id+"F0.wireOp",EDGE,"E1.top"),sQuery(id+"F0.wireOp",EDGE,"E1.left"),sQuery(id+"F0.wireOp",EDGE,"E1.right"),sQuery(id+"F0.wireOp",EDGE,"E2.top"),sQuery(id+"F0.wireOp",EDGE,"E2.left"),sQuery(id+"F0.wireOp",EDGE,"E2.right"),sQuery(id+"F0.wireOp",EDGE,"E3.top"),sQuery(id+"F0.wireOp",EDGE,"E3.left"),sQuery(id+"F0.wireOp",EDGE,"E3.right"),sQuery(id+"F0.wireOp",EDGE,"E4.top"),sQuery(id+"F0.wireOp",EDGE,"E4.left"),sQuery(id+"F0.wireOp",EDGE,"E4.right"),sQuery(id+"F0.wireOp",EDGE,"E5.top"),sQuery(id+"F0.wireOp",EDGE,"E5.left"),sQuery(id+"F0.wireOp",EDGE,"E5.right"),sQuery(id+"F0.wireOp",EDGE,"E6.top"),sQuery(id+"F0.wireOp",EDGE,"E6.left"),sQuery(id+"F0.wireOp",EDGE,"E6.right"),sQuery(id+"F0.wireOp",EDGE,"E7.top"),sQuery(id+"F0.wireOp",EDGE,"E7.left"),sQuery(id+"F0.wireOp",EDGE,"E7.right"),sQuery(id+"F0.wireOp",EDGE,"E8.top"),sQuery(id+"F0.wireOp",EDGE,"E8.left"),sQuery(id+"F0.wireOp",EDGE,"E8.right"),sQuery(id+"F0.wireOp",EDGE,"E9.top"),sQuery(id+"F0.wireOp",EDGE,"E9.left"),sQuery(id+"F0.wireOp",EDGE,"E9.right"),sQuery(id+"F0.wireOp",EDGE,"E10.top"),sQuery(id+"F0.wireOp",EDGE,"E10.left"),sQuery(id+"F0.wireOp",EDGE,"E10.right"),sQuery(id+"F0.wireOp",EDGE,"E11.filletArc"),sQuery(id+"F0.wireOp",EDGE,"E12.filletArc"),sQuery(id+"F0.wireOp",EDGE,"E13.filletArc"),sQuery(id+"F0.wireOp",EDGE,"E14.filletArc"),sQuery(id+"F0.wireOp",EDGE,"E17"),sQuery(id+"F0.wireOp",EDGE,"E18"),sQuery(id+"F0.wireOp",EDGE,"E19"),sQuery(id+"F0.wireOp",EDGE,"E21")])]}),"instanceName":"1"});
            transform(context, id + "F4", {"entities" : qUnion([Q0, Q1, Q2, Q3, Q4, Q5, Q6, Q7, Q8]), "transformType" : TransformType.TRANSLATION_3D, "dx" : 0 * mm, "dy" : -6 * mm, "dz" : 0 * mm, "makeCopy" : false});
        }
        {
            var Q0;
            Q0=makeQuery(id+"FeItU8t7BcqmXxs_1.opPattern","COPY",BODY,{"derivedFrom":makeQuery(id+"FirfgJDHHkA21Hh_1.opPattern","COPY",BODY,{"derivedFrom":makeQuery(id+"Flst8gmBcSAihEz_1.opPattern","COPY",BODY,{"derivedFrom":makeQuery(id+"FnchQCX3KFHkyZE_1.opPattern","COPY",BODY,{"derivedFrom":makeQuery(id+"FnXCqMF8rCCX5tp_1.opPattern","COPY",BODY,{"derivedFrom":makeQuery(id+"FpTvk6VpooPmInK_1.opPattern","COPY",BODY,{"derivedFrom":makeQuery(id+"FDAv0ZJfrHdLi5i_1.opPattern","COPY",BODY,{"derivedFrom":makeQuery(id+"FECZTDOQryJ9ywm_1.opPattern","COPY",BODY,{"derivedFrom":makeQuery(id+"F1.opExtrude","SWEPT_BODY",BODY,{"disambiguationData":[OSD([sQuery(id+"F0.wireOp",EDGE,"E0.bottom"),sQuery(id+"F0.wireOp",EDGE,"E0.top"),sQuery(id+"F0.wireOp",EDGE,"E0.left"),sQuery(id+"F0.wireOp",EDGE,"E0.right"),sQuery(id+"F0.wireOp",EDGE,"E1.top"),sQuery(id+"F0.wireOp",EDGE,"E1.left"),sQuery(id+"F0.wireOp",EDGE,"E1.right"),sQuery(id+"F0.wireOp",EDGE,"E2.top"),sQuery(id+"F0.wireOp",EDGE,"E2.left"),sQuery(id+"F0.wireOp",EDGE,"E2.right"),sQuery(id+"F0.wireOp",EDGE,"E3.top"),sQuery(id+"F0.wireOp",EDGE,"E3.left"),sQuery(id+"F0.wireOp",EDGE,"E3.right"),sQuery(id+"F0.wireOp",EDGE,"E4.top"),sQuery(id+"F0.wireOp",EDGE,"E4.left"),sQuery(id+"F0.wireOp",EDGE,"E4.right"),sQuery(id+"F0.wireOp",EDGE,"E5.top"),sQuery(id+"F0.wireOp",EDGE,"E5.left"),sQuery(id+"F0.wireOp",EDGE,"E5.right"),sQuery(id+"F0.wireOp",EDGE,"E6.top"),sQuery(id+"F0.wireOp",EDGE,"E6.left"),sQuery(id+"F0.wireOp",EDGE,"E6.right"),sQuery(id+"F0.wireOp",EDGE,"E7.top"),sQuery(id+"F0.wireOp",EDGE,"E7.left"),sQuery(id+"F0.wireOp",EDGE,"E7.right"),sQuery(id+"F0.wireOp",EDGE,"E8.top"),sQuery(id+"F0.wireOp",EDGE,"E8.left"),sQuery(id+"F0.wireOp",EDGE,"E8.right"),sQuery(id+"F0.wireOp",EDGE,"E9.top"),sQuery(id+"F0.wireOp",EDGE,"E9.left"),sQuery(id+"F0.wireOp",EDGE,"E9.right"),sQuery(id+"F0.wireOp",EDGE,"E10.top"),sQuery(id+"F0.wireOp",EDGE,"E10.left"),sQuery(id+"F0.wireOp",EDGE,"E10.right"),sQuery(id+"F0.wireOp",EDGE,"E11.filletArc"),sQuery(id+"F0.wireOp",EDGE,"E12.filletArc"),sQuery(id+"F0.wireOp",EDGE,"E13.filletArc"),sQuery(id+"F0.wireOp",EDGE,"E14.filletArc"),sQuery(id+"F0.wireOp",EDGE,"E17"),sQuery(id+"F0.wireOp",EDGE,"E18"),sQuery(id+"F0.wireOp",EDGE,"E19"),sQuery(id+"F0.wireOp",EDGE,"E21")])]}),"instanceName":"1"}),"instanceName":"1"}),"instanceName":"1"}),"instanceName":"1"}),"instanceName":"1"}),"instanceName":"1"}),"instanceName":"1"}),"instanceName":"1"});
            var Q1;
            Q1=makeQuery(id+"FirfgJDHHkA21Hh_1.opPattern","COPY",BODY,{"derivedFrom":makeQuery(id+"Flst8gmBcSAihEz_1.opPattern","COPY",BODY,{"derivedFrom":makeQuery(id+"FnchQCX3KFHkyZE_1.opPattern","COPY",BODY,{"derivedFrom":makeQuery(id+"FnXCqMF8rCCX5tp_1.opPattern","COPY",BODY,{"derivedFrom":makeQuery(id+"FpTvk6VpooPmInK_1.opPattern","COPY",BODY,{"derivedFrom":makeQuery(id+"FDAv0ZJfrHdLi5i_1.opPattern","COPY",BODY,{"derivedFrom":makeQuery(id+"FECZTDOQryJ9ywm_1.opPattern","COPY",BODY,{"derivedFrom":makeQuery(id+"F1.opExtrude","SWEPT_BODY",BODY,{"disambiguationData":[OSD([sQuery(id+"F0.wireOp",EDGE,"E0.bottom"),sQuery(id+"F0.wireOp",EDGE,"E0.top"),sQuery(id+"F0.wireOp",EDGE,"E0.left"),sQuery(id+"F0.wireOp",EDGE,"E0.right"),sQuery(id+"F0.wireOp",EDGE,"E1.top"),sQuery(id+"F0.wireOp",EDGE,"E1.left"),sQuery(id+"F0.wireOp",EDGE,"E1.right"),sQuery(id+"F0.wireOp",EDGE,"E2.top"),sQuery(id+"F0.wireOp",EDGE,"E2.left"),sQuery(id+"F0.wireOp",EDGE,"E2.right"),sQuery(id+"F0.wireOp",EDGE,"E3.top"),sQuery(id+"F0.wireOp",EDGE,"E3.left"),sQuery(id+"F0.wireOp",EDGE,"E3.right"),sQuery(id+"F0.wireOp",EDGE,"E4.top"),sQuery(id+"F0.wireOp",EDGE,"E4.left"),sQuery(id+"F0.wireOp",EDGE,"E4.right"),sQuery(id+"F0.wireOp",EDGE,"E5.top"),sQuery(id+"F0.wireOp",EDGE,"E5.left"),sQuery(id+"F0.wireOp",EDGE,"E5.right"),sQuery(id+"F0.wireOp",EDGE,"E6.top"),sQuery(id+"F0.wireOp",EDGE,"E6.left"),sQuery(id+"F0.wireOp",EDGE,"E6.right"),sQuery(id+"F0.wireOp",EDGE,"E7.top"),sQuery(id+"F0.wireOp",EDGE,"E7.left"),sQuery(id+"F0.wireOp",EDGE,"E7.right"),sQuery(id+"F0.wireOp",EDGE,"E8.top"),sQuery(id+"F0.wireOp",EDGE,"E8.left"),sQuery(id+"F0.wireOp",EDGE,"E8.right"),sQuery(id+"F0.wireOp",EDGE,"E9.top"),sQuery(id+"F0.wireOp",EDGE,"E9.left"),sQuery(id+"F0.wireOp",EDGE,"E9.right"),sQuery(id+"F0.wireOp",EDGE,"E10.top"),sQuery(id+"F0.wireOp",EDGE,"E10.left"),sQuery(id+"F0.wireOp",EDGE,"E10.right"),sQuery(id+"F0.wireOp",EDGE,"E11.filletArc"),sQuery(id+"F0.wireOp",EDGE,"E12.filletArc"),sQuery(id+"F0.wireOp",EDGE,"E13.filletArc"),sQuery(id+"F0.wireOp",EDGE,"E14.filletArc"),sQuery(id+"F0.wireOp",EDGE,"E17"),sQuery(id+"F0.wireOp",EDGE,"E18"),sQuery(id+"F0.wireOp",EDGE,"E19"),sQuery(id+"F0.wireOp",EDGE,"E21")])]}),"instanceName":"1"}),"instanceName":"1"}),"instanceName":"1"}),"instanceName":"1"}),"instanceName":"1"}),"instanceName":"1"}),"instanceName":"1"});
            var Q2;
            Q2=makeQuery(id+"Flst8gmBcSAihEz_1.opPattern","COPY",BODY,{"derivedFrom":makeQuery(id+"FnchQCX3KFHkyZE_1.opPattern","COPY",BODY,{"derivedFrom":makeQuery(id+"FnXCqMF8rCCX5tp_1.opPattern","COPY",BODY,{"derivedFrom":makeQuery(id+"FpTvk6VpooPmInK_1.opPattern","COPY",BODY,{"derivedFrom":makeQuery(id+"FDAv0ZJfrHdLi5i_1.opPattern","COPY",BODY,{"derivedFrom":makeQuery(id+"FECZTDOQryJ9ywm_1.opPattern","COPY",BODY,{"derivedFrom":makeQuery(id+"F1.opExtrude","SWEPT_BODY",BODY,{"disambiguationData":[OSD([sQuery(id+"F0.wireOp",EDGE,"E0.bottom"),sQuery(id+"F0.wireOp",EDGE,"E0.top"),sQuery(id+"F0.wireOp",EDGE,"E0.left"),sQuery(id+"F0.wireOp",EDGE,"E0.right"),sQuery(id+"F0.wireOp",EDGE,"E1.top"),sQuery(id+"F0.wireOp",EDGE,"E1.left"),sQuery(id+"F0.wireOp",EDGE,"E1.right"),sQuery(id+"F0.wireOp",EDGE,"E2.top"),sQuery(id+"F0.wireOp",EDGE,"E2.left"),sQuery(id+"F0.wireOp",EDGE,"E2.right"),sQuery(id+"F0.wireOp",EDGE,"E3.top"),sQuery(id+"F0.wireOp",EDGE,"E3.left"),sQuery(id+"F0.wireOp",EDGE,"E3.right"),sQuery(id+"F0.wireOp",EDGE,"E4.top"),sQuery(id+"F0.wireOp",EDGE,"E4.left"),sQuery(id+"F0.wireOp",EDGE,"E4.right"),sQuery(id+"F0.wireOp",EDGE,"E5.top"),sQuery(id+"F0.wireOp",EDGE,"E5.left"),sQuery(id+"F0.wireOp",EDGE,"E5.right"),sQuery(id+"F0.wireOp",EDGE,"E6.top"),sQuery(id+"F0.wireOp",EDGE,"E6.left"),sQuery(id+"F0.wireOp",EDGE,"E6.right"),sQuery(id+"F0.wireOp",EDGE,"E7.top"),sQuery(id+"F0.wireOp",EDGE,"E7.left"),sQuery(id+"F0.wireOp",EDGE,"E7.right"),sQuery(id+"F0.wireOp",EDGE,"E8.top"),sQuery(id+"F0.wireOp",EDGE,"E8.left"),sQuery(id+"F0.wireOp",EDGE,"E8.right"),sQuery(id+"F0.wireOp",EDGE,"E9.top"),sQuery(id+"F0.wireOp",EDGE,"E9.left"),sQuery(id+"F0.wireOp",EDGE,"E9.right"),sQuery(id+"F0.wireOp",EDGE,"E10.top"),sQuery(id+"F0.wireOp",EDGE,"E10.left"),sQuery(id+"F0.wireOp",EDGE,"E10.right"),sQuery(id+"F0.wireOp",EDGE,"E11.filletArc"),sQuery(id+"F0.wireOp",EDGE,"E12.filletArc"),sQuery(id+"F0.wireOp",EDGE,"E13.filletArc"),sQuery(id+"F0.wireOp",EDGE,"E14.filletArc"),sQuery(id+"F0.wireOp",EDGE,"E17"),sQuery(id+"F0.wireOp",EDGE,"E18"),sQuery(id+"F0.wireOp",EDGE,"E19"),sQuery(id+"F0.wireOp",EDGE,"E21")])]}),"instanceName":"1"}),"instanceName":"1"}),"instanceName":"1"}),"instanceName":"1"}),"instanceName":"1"}),"instanceName":"1"});
            var Q3;
            Q3=makeQuery(id+"FnchQCX3KFHkyZE_1.opPattern","COPY",BODY,{"derivedFrom":makeQuery(id+"FnXCqMF8rCCX5tp_1.opPattern","COPY",BODY,{"derivedFrom":makeQuery(id+"FpTvk6VpooPmInK_1.opPattern","COPY",BODY,{"derivedFrom":makeQuery(id+"FDAv0ZJfrHdLi5i_1.opPattern","COPY",BODY,{"derivedFrom":makeQuery(id+"FECZTDOQryJ9ywm_1.opPattern","COPY",BODY,{"derivedFrom":makeQuery(id+"F1.opExtrude","SWEPT_BODY",BODY,{"disambiguationData":[OSD([sQuery(id+"F0.wireOp",EDGE,"E0.bottom"),sQuery(id+"F0.wireOp",EDGE,"E0.top"),sQuery(id+"F0.wireOp",EDGE,"E0.left"),sQuery(id+"F0.wireOp",EDGE,"E0.right"),sQuery(id+"F0.wireOp",EDGE,"E1.top"),sQuery(id+"F0.wireOp",EDGE,"E1.left"),sQuery(id+"F0.wireOp",EDGE,"E1.right"),sQuery(id+"F0.wireOp",EDGE,"E2.top"),sQuery(id+"F0.wireOp",EDGE,"E2.left"),sQuery(id+"F0.wireOp",EDGE,"E2.right"),sQuery(id+"F0.wireOp",EDGE,"E3.top"),sQuery(id+"F0.wireOp",EDGE,"E3.left"),sQuery(id+"F0.wireOp",EDGE,"E3.right"),sQuery(id+"F0.wireOp",EDGE,"E4.top"),sQuery(id+"F0.wireOp",EDGE,"E4.left"),sQuery(id+"F0.wireOp",EDGE,"E4.right"),sQuery(id+"F0.wireOp",EDGE,"E5.top"),sQuery(id+"F0.wireOp",EDGE,"E5.left"),sQuery(id+"F0.wireOp",EDGE,"E5.right"),sQuery(id+"F0.wireOp",EDGE,"E6.top"),sQuery(id+"F0.wireOp",EDGE,"E6.left"),sQuery(id+"F0.wireOp",EDGE,"E6.right"),sQuery(id+"F0.wireOp",EDGE,"E7.top"),sQuery(id+"F0.wireOp",EDGE,"E7.left"),sQuery(id+"F0.wireOp",EDGE,"E7.right"),sQuery(id+"F0.wireOp",EDGE,"E8.top"),sQuery(id+"F0.wireOp",EDGE,"E8.left"),sQuery(id+"F0.wireOp",EDGE,"E8.right"),sQuery(id+"F0.wireOp",EDGE,"E9.top"),sQuery(id+"F0.wireOp",EDGE,"E9.left"),sQuery(id+"F0.wireOp",EDGE,"E9.right"),sQuery(id+"F0.wireOp",EDGE,"E10.top"),sQuery(id+"F0.wireOp",EDGE,"E10.left"),sQuery(id+"F0.wireOp",EDGE,"E10.right"),sQuery(id+"F0.wireOp",EDGE,"E11.filletArc"),sQuery(id+"F0.wireOp",EDGE,"E12.filletArc"),sQuery(id+"F0.wireOp",EDGE,"E13.filletArc"),sQuery(id+"F0.wireOp",EDGE,"E14.filletArc"),sQuery(id+"F0.wireOp",EDGE,"E17"),sQuery(id+"F0.wireOp",EDGE,"E18"),sQuery(id+"F0.wireOp",EDGE,"E19"),sQuery(id+"F0.wireOp",EDGE,"E21")])]}),"instanceName":"1"}),"instanceName":"1"}),"instanceName":"1"}),"instanceName":"1"}),"instanceName":"1"});
            var Q4;
            Q4=makeQuery(id+"FnXCqMF8rCCX5tp_1.opPattern","COPY",BODY,{"derivedFrom":makeQuery(id+"FpTvk6VpooPmInK_1.opPattern","COPY",BODY,{"derivedFrom":makeQuery(id+"FDAv0ZJfrHdLi5i_1.opPattern","COPY",BODY,{"derivedFrom":makeQuery(id+"FECZTDOQryJ9ywm_1.opPattern","COPY",BODY,{"derivedFrom":makeQuery(id+"F1.opExtrude","SWEPT_BODY",BODY,{"disambiguationData":[OSD([sQuery(id+"F0.wireOp",EDGE,"E0.bottom"),sQuery(id+"F0.wireOp",EDGE,"E0.top"),sQuery(id+"F0.wireOp",EDGE,"E0.left"),sQuery(id+"F0.wireOp",EDGE,"E0.right"),sQuery(id+"F0.wireOp",EDGE,"E1.top"),sQuery(id+"F0.wireOp",EDGE,"E1.left"),sQuery(id+"F0.wireOp",EDGE,"E1.right"),sQuery(id+"F0.wireOp",EDGE,"E2.top"),sQuery(id+"F0.wireOp",EDGE,"E2.left"),sQuery(id+"F0.wireOp",EDGE,"E2.right"),sQuery(id+"F0.wireOp",EDGE,"E3.top"),sQuery(id+"F0.wireOp",EDGE,"E3.left"),sQuery(id+"F0.wireOp",EDGE,"E3.right"),sQuery(id+"F0.wireOp",EDGE,"E4.top"),sQuery(id+"F0.wireOp",EDGE,"E4.left"),sQuery(id+"F0.wireOp",EDGE,"E4.right"),sQuery(id+"F0.wireOp",EDGE,"E5.top"),sQuery(id+"F0.wireOp",EDGE,"E5.left"),sQuery(id+"F0.wireOp",EDGE,"E5.right"),sQuery(id+"F0.wireOp",EDGE,"E6.top"),sQuery(id+"F0.wireOp",EDGE,"E6.left"),sQuery(id+"F0.wireOp",EDGE,"E6.right"),sQuery(id+"F0.wireOp",EDGE,"E7.top"),sQuery(id+"F0.wireOp",EDGE,"E7.left"),sQuery(id+"F0.wireOp",EDGE,"E7.right"),sQuery(id+"F0.wireOp",EDGE,"E8.top"),sQuery(id+"F0.wireOp",EDGE,"E8.left"),sQuery(id+"F0.wireOp",EDGE,"E8.right"),sQuery(id+"F0.wireOp",EDGE,"E9.top"),sQuery(id+"F0.wireOp",EDGE,"E9.left"),sQuery(id+"F0.wireOp",EDGE,"E9.right"),sQuery(id+"F0.wireOp",EDGE,"E10.top"),sQuery(id+"F0.wireOp",EDGE,"E10.left"),sQuery(id+"F0.wireOp",EDGE,"E10.right"),sQuery(id+"F0.wireOp",EDGE,"E11.filletArc"),sQuery(id+"F0.wireOp",EDGE,"E12.filletArc"),sQuery(id+"F0.wireOp",EDGE,"E13.filletArc"),sQuery(id+"F0.wireOp",EDGE,"E14.filletArc"),sQuery(id+"F0.wireOp",EDGE,"E17"),sQuery(id+"F0.wireOp",EDGE,"E18"),sQuery(id+"F0.wireOp",EDGE,"E19"),sQuery(id+"F0.wireOp",EDGE,"E21")])]}),"instanceName":"1"}),"instanceName":"1"}),"instanceName":"1"}),"instanceName":"1"});
            var Q5;
            Q5=makeQuery(id+"F1.opExtrude","SWEPT_BODY",BODY,{"disambiguationData":[OSD([sQuery(id+"F0.wireOp",EDGE,"E0.bottom"),sQuery(id+"F0.wireOp",EDGE,"E0.top"),sQuery(id+"F0.wireOp",EDGE,"E0.left"),sQuery(id+"F0.wireOp",EDGE,"E0.right"),sQuery(id+"F0.wireOp",EDGE,"E1.top"),sQuery(id+"F0.wireOp",EDGE,"E1.left"),sQuery(id+"F0.wireOp",EDGE,"E1.right"),sQuery(id+"F0.wireOp",EDGE,"E2.top"),sQuery(id+"F0.wireOp",EDGE,"E2.left"),sQuery(id+"F0.wireOp",EDGE,"E2.right"),sQuery(id+"F0.wireOp",EDGE,"E3.top"),sQuery(id+"F0.wireOp",EDGE,"E3.left"),sQuery(id+"F0.wireOp",EDGE,"E3.right"),sQuery(id+"F0.wireOp",EDGE,"E4.top"),sQuery(id+"F0.wireOp",EDGE,"E4.left"),sQuery(id+"F0.wireOp",EDGE,"E4.right"),sQuery(id+"F0.wireOp",EDGE,"E5.top"),sQuery(id+"F0.wireOp",EDGE,"E5.left"),sQuery(id+"F0.wireOp",EDGE,"E5.right"),sQuery(id+"F0.wireOp",EDGE,"E6.top"),sQuery(id+"F0.wireOp",EDGE,"E6.left"),sQuery(id+"F0.wireOp",EDGE,"E6.right"),sQuery(id+"F0.wireOp",EDGE,"E7.top"),sQuery(id+"F0.wireOp",EDGE,"E7.left"),sQuery(id+"F0.wireOp",EDGE,"E7.right"),sQuery(id+"F0.wireOp",EDGE,"E8.top"),sQuery(id+"F0.wireOp",EDGE,"E8.left"),sQuery(id+"F0.wireOp",EDGE,"E8.right"),sQuery(id+"F0.wireOp",EDGE,"E9.top"),sQuery(id+"F0.wireOp",EDGE,"E9.left"),sQuery(id+"F0.wireOp",EDGE,"E9.right"),sQuery(id+"F0.wireOp",EDGE,"E10.top"),sQuery(id+"F0.wireOp",EDGE,"E10.left"),sQuery(id+"F0.wireOp",EDGE,"E10.right"),sQuery(id+"F0.wireOp",EDGE,"E11.filletArc"),sQuery(id+"F0.wireOp",EDGE,"E12.filletArc"),sQuery(id+"F0.wireOp",EDGE,"E13.filletArc"),sQuery(id+"F0.wireOp",EDGE,"E14.filletArc"),sQuery(id+"F0.wireOp",EDGE,"E17"),sQuery(id+"F0.wireOp",EDGE,"E18"),sQuery(id+"F0.wireOp",EDGE,"E19"),sQuery(id+"F0.wireOp",EDGE,"E21")])]});
            var Q6;
            Q6=makeQuery(id+"FpTvk6VpooPmInK_1.opPattern","COPY",BODY,{"derivedFrom":makeQuery(id+"FDAv0ZJfrHdLi5i_1.opPattern","COPY",BODY,{"derivedFrom":makeQuery(id+"FECZTDOQryJ9ywm_1.opPattern","COPY",BODY,{"derivedFrom":makeQuery(id+"F1.opExtrude","SWEPT_BODY",BODY,{"disambiguationData":[OSD([sQuery(id+"F0.wireOp",EDGE,"E0.bottom"),sQuery(id+"F0.wireOp",EDGE,"E0.top"),sQuery(id+"F0.wireOp",EDGE,"E0.left"),sQuery(id+"F0.wireOp",EDGE,"E0.right"),sQuery(id+"F0.wireOp",EDGE,"E1.top"),sQuery(id+"F0.wireOp",EDGE,"E1.left"),sQuery(id+"F0.wireOp",EDGE,"E1.right"),sQuery(id+"F0.wireOp",EDGE,"E2.top"),sQuery(id+"F0.wireOp",EDGE,"E2.left"),sQuery(id+"F0.wireOp",EDGE,"E2.right"),sQuery(id+"F0.wireOp",EDGE,"E3.top"),sQuery(id+"F0.wireOp",EDGE,"E3.left"),sQuery(id+"F0.wireOp",EDGE,"E3.right"),sQuery(id+"F0.wireOp",EDGE,"E4.top"),sQuery(id+"F0.wireOp",EDGE,"E4.left"),sQuery(id+"F0.wireOp",EDGE,"E4.right"),sQuery(id+"F0.wireOp",EDGE,"E5.top"),sQuery(id+"F0.wireOp",EDGE,"E5.left"),sQuery(id+"F0.wireOp",EDGE,"E5.right"),sQuery(id+"F0.wireOp",EDGE,"E6.top"),sQuery(id+"F0.wireOp",EDGE,"E6.left"),sQuery(id+"F0.wireOp",EDGE,"E6.right"),sQuery(id+"F0.wireOp",EDGE,"E7.top"),sQuery(id+"F0.wireOp",EDGE,"E7.left"),sQuery(id+"F0.wireOp",EDGE,"E7.right"),sQuery(id+"F0.wireOp",EDGE,"E8.top"),sQuery(id+"F0.wireOp",EDGE,"E8.left"),sQuery(id+"F0.wireOp",EDGE,"E8.right"),sQuery(id+"F0.wireOp",EDGE,"E9.top"),sQuery(id+"F0.wireOp",EDGE,"E9.left"),sQuery(id+"F0.wireOp",EDGE,"E9.right"),sQuery(id+"F0.wireOp",EDGE,"E10.top"),sQuery(id+"F0.wireOp",EDGE,"E10.left"),sQuery(id+"F0.wireOp",EDGE,"E10.right"),sQuery(id+"F0.wireOp",EDGE,"E11.filletArc"),sQuery(id+"F0.wireOp",EDGE,"E12.filletArc"),sQuery(id+"F0.wireOp",EDGE,"E13.filletArc"),sQuery(id+"F0.wireOp",EDGE,"E14.filletArc"),sQuery(id+"F0.wireOp",EDGE,"E17"),sQuery(id+"F0.wireOp",EDGE,"E18"),sQuery(id+"F0.wireOp",EDGE,"E19"),sQuery(id+"F0.wireOp",EDGE,"E21")])]}),"instanceName":"1"}),"instanceName":"1"}),"instanceName":"1"});
            var Q7;
            Q7=makeQuery(id+"FDAv0ZJfrHdLi5i_1.opPattern","COPY",BODY,{"derivedFrom":makeQuery(id+"FECZTDOQryJ9ywm_1.opPattern","COPY",BODY,{"derivedFrom":makeQuery(id+"F1.opExtrude","SWEPT_BODY",BODY,{"disambiguationData":[OSD([sQuery(id+"F0.wireOp",EDGE,"E0.bottom"),sQuery(id+"F0.wireOp",EDGE,"E0.top"),sQuery(id+"F0.wireOp",EDGE,"E0.left"),sQuery(id+"F0.wireOp",EDGE,"E0.right"),sQuery(id+"F0.wireOp",EDGE,"E1.top"),sQuery(id+"F0.wireOp",EDGE,"E1.left"),sQuery(id+"F0.wireOp",EDGE,"E1.right"),sQuery(id+"F0.wireOp",EDGE,"E2.top"),sQuery(id+"F0.wireOp",EDGE,"E2.left"),sQuery(id+"F0.wireOp",EDGE,"E2.right"),sQuery(id+"F0.wireOp",EDGE,"E3.top"),sQuery(id+"F0.wireOp",EDGE,"E3.left"),sQuery(id+"F0.wireOp",EDGE,"E3.right"),sQuery(id+"F0.wireOp",EDGE,"E4.top"),sQuery(id+"F0.wireOp",EDGE,"E4.left"),sQuery(id+"F0.wireOp",EDGE,"E4.right"),sQuery(id+"F0.wireOp",EDGE,"E5.top"),sQuery(id+"F0.wireOp",EDGE,"E5.left"),sQuery(id+"F0.wireOp",EDGE,"E5.right"),sQuery(id+"F0.wireOp",EDGE,"E6.top"),sQuery(id+"F0.wireOp",EDGE,"E6.left"),sQuery(id+"F0.wireOp",EDGE,"E6.right"),sQuery(id+"F0.wireOp",EDGE,"E7.top"),sQuery(id+"F0.wireOp",EDGE,"E7.left"),sQuery(id+"F0.wireOp",EDGE,"E7.right"),sQuery(id+"F0.wireOp",EDGE,"E8.top"),sQuery(id+"F0.wireOp",EDGE,"E8.left"),sQuery(id+"F0.wireOp",EDGE,"E8.right"),sQuery(id+"F0.wireOp",EDGE,"E9.top"),sQuery(id+"F0.wireOp",EDGE,"E9.left"),sQuery(id+"F0.wireOp",EDGE,"E9.right"),sQuery(id+"F0.wireOp",EDGE,"E10.top"),sQuery(id+"F0.wireOp",EDGE,"E10.left"),sQuery(id+"F0.wireOp",EDGE,"E10.right"),sQuery(id+"F0.wireOp",EDGE,"E11.filletArc"),sQuery(id+"F0.wireOp",EDGE,"E12.filletArc"),sQuery(id+"F0.wireOp",EDGE,"E13.filletArc"),sQuery(id+"F0.wireOp",EDGE,"E14.filletArc"),sQuery(id+"F0.wireOp",EDGE,"E17"),sQuery(id+"F0.wireOp",EDGE,"E18"),sQuery(id+"F0.wireOp",EDGE,"E19"),sQuery(id+"F0.wireOp",EDGE,"E21")])]}),"instanceName":"1"}),"instanceName":"1"});
            var Q8;
            Q8=makeQuery(id+"FECZTDOQryJ9ywm_1.opPattern","COPY",BODY,{"derivedFrom":makeQuery(id+"F1.opExtrude","SWEPT_BODY",BODY,{"disambiguationData":[OSD([sQuery(id+"F0.wireOp",EDGE,"E0.bottom"),sQuery(id+"F0.wireOp",EDGE,"E0.top"),sQuery(id+"F0.wireOp",EDGE,"E0.left"),sQuery(id+"F0.wireOp",EDGE,"E0.right"),sQuery(id+"F0.wireOp",EDGE,"E1.top"),sQuery(id+"F0.wireOp",EDGE,"E1.left"),sQuery(id+"F0.wireOp",EDGE,"E1.right"),sQuery(id+"F0.wireOp",EDGE,"E2.top"),sQuery(id+"F0.wireOp",EDGE,"E2.left"),sQuery(id+"F0.wireOp",EDGE,"E2.right"),sQuery(id+"F0.wireOp",EDGE,"E3.top"),sQuery(id+"F0.wireOp",EDGE,"E3.left"),sQuery(id+"F0.wireOp",EDGE,"E3.right"),sQuery(id+"F0.wireOp",EDGE,"E4.top"),sQuery(id+"F0.wireOp",EDGE,"E4.left"),sQuery(id+"F0.wireOp",EDGE,"E4.right"),sQuery(id+"F0.wireOp",EDGE,"E5.top"),sQuery(id+"F0.wireOp",EDGE,"E5.left"),sQuery(id+"F0.wireOp",EDGE,"E5.right"),sQuery(id+"F0.wireOp",EDGE,"E6.top"),sQuery(id+"F0.wireOp",EDGE,"E6.left"),sQuery(id+"F0.wireOp",EDGE,"E6.right"),sQuery(id+"F0.wireOp",EDGE,"E7.top"),sQuery(id+"F0.wireOp",EDGE,"E7.left"),sQuery(id+"F0.wireOp",EDGE,"E7.right"),sQuery(id+"F0.wireOp",EDGE,"E8.top"),sQuery(id+"F0.wireOp",EDGE,"E8.left"),sQuery(id+"F0.wireOp",EDGE,"E8.right"),sQuery(id+"F0.wireOp",EDGE,"E9.top"),sQuery(id+"F0.wireOp",EDGE,"E9.left"),sQuery(id+"F0.wireOp",EDGE,"E9.right"),sQuery(id+"F0.wireOp",EDGE,"E10.top"),sQuery(id+"F0.wireOp",EDGE,"E10.left"),sQuery(id+"F0.wireOp",EDGE,"E10.right"),sQuery(id+"F0.wireOp",EDGE,"E11.filletArc"),sQuery(id+"F0.wireOp",EDGE,"E12.filletArc"),sQuery(id+"F0.wireOp",EDGE,"E13.filletArc"),sQuery(id+"F0.wireOp",EDGE,"E14.filletArc"),sQuery(id+"F0.wireOp",EDGE,"E17"),sQuery(id+"F0.wireOp",EDGE,"E18"),sQuery(id+"F0.wireOp",EDGE,"E19"),sQuery(id+"F0.wireOp",EDGE,"E21")])]}),"instanceName":"1"});
            transform(context, id + "F5", {"entities" : qUnion([Q0, Q1, Q2, Q3, Q4, Q5, Q6, Q7, Q8]), "transformType" : TransformType.TRANSLATION_3D, "dx" : -1 * mm, "dy" : 0 * mm, "dz" : 0 * mm, "makeCopy" : false});
        }
    });
